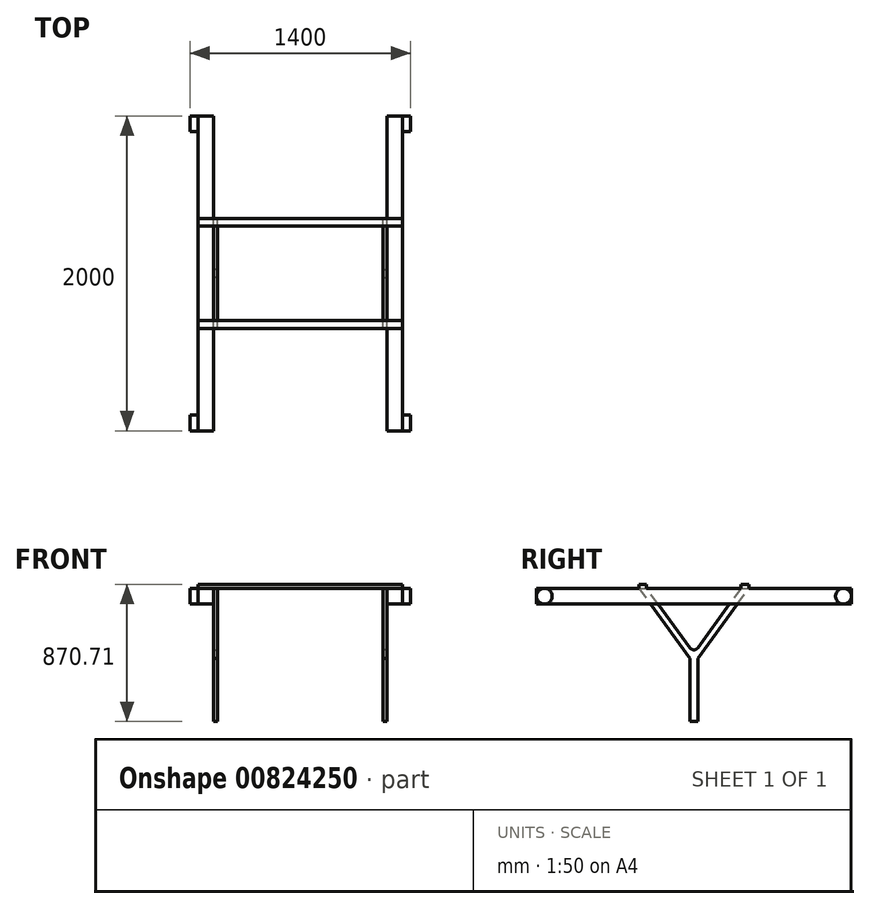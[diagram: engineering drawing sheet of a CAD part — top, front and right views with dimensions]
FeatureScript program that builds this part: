
annotation { "Feature Type Name" : "Feature", "Feature Type Description" : "" }
export const myFeature = defineFeature(function(context is Context, id is Id, definition is map)
    precondition{}
    {
        {
            var Q0;
            Q0=qCreatedBy(makeId("Top.planeOp"),FACE);
            var sketch = newSketch(context, id + "F0", { "sketchPlane" : qUnion([Q0])});
            skLineSegment(sketch, "E0.bottom", {"start": v(650, -1000) * mm, "end": v(550, -1000) * mm});
            skLineSegment(sketch, "E0.top", {"start": v(650, 1000) * mm, "end": v(550, 1000) * mm});
            skLineSegment(sketch, "E0.left", {"start": v(650, -1000) * mm, "end": v(650, 1000) * mm});
            skLineSegment(sketch, "E0.right", {"start": v(-650, -1000) * mm, "end": v(-650, 1000) * mm});
            skPoint(sketch, "E0.middle", {"position": v(0, 0) * mm});
            skLineSegment(sketch, "E1.left", {"start": v(-550, -1000) * mm, "end": v(-550, 1000) * mm});
            skLineSegment(sketch, "E1.right", {"start": v(550, -1000) * mm, "end": v(550, 1000) * mm});
            skLineSegment(sketch, "E2.trimOffspring", {"start": v(-550, 1000) * mm, "end": v(-650, 1000) * mm});
            skLineSegment(sketch, "E3.trimOffspring", {"start": v(-550, -1000) * mm, "end": v(-650, -1000) * mm});
            skSolve(sketch);
        }
        {
            var Q0;
            Q0 = qSketchRegion(id + "F0", true);
            extrude(context, id + "F1", {"entities" : qUnion([Q0]), "depth" : 100 * mm, "offsetDistance" : 25 * mm});
        }
        {
            var Q0;
            Q0=makeQuery(id+"F1.opExtrude","CAP_FACE",FACE,{"disambiguationData":[OSD([sQuery(id+"F0.wireOp",EDGE,"E0.bottom"),sQuery(id+"F0.wireOp",EDGE,"E0.top"),sQuery(id+"F0.wireOp",EDGE,"E0.left"),sQuery(id+"F0.wireOp",EDGE,"E1.right")])],"isStart":false});
            var sketch = newSketch(context, id + "F2", { "sketchPlane" : qUnion([Q0])});
            skLineSegment(sketch, "E4.bottom", {"start": v(650, -350) * mm, "end": v(-650, -350) * mm});
            skLineSegment(sketch, "E4.top", {"start": v(650, -300) * mm, "end": v(-650, -300) * mm});
            skLineSegment(sketch, "E4.left", {"start": v(650, -350) * mm, "end": v(650, -300) * mm});
            skLineSegment(sketch, "E4.right", {"start": v(-650, -350) * mm, "end": v(-650, -300) * mm});
            skLineSegment(sketch, "E5.MirrorCS", {"start": v(-650, 350) * mm, "end": v(-650, 300) * mm});
            skLineSegment(sketch, "E6.MirrorCS", {"start": v(650, 350) * mm, "end": v(650, 300) * mm});
            skLineSegment(sketch, "E7.MirrorCS", {"start": v(650, 300) * mm, "end": v(-650, 300) * mm});
            skLineSegment(sketch, "E8.MirrorCS", {"start": v(650, 350) * mm, "end": v(-650, 350) * mm});
            skSolve(sketch);
        }
        {
            var Q0;
            Q0 = qSketchRegion(id + "F2", true);
            extrude(context, id + "F3", {"entities" : qUnion([Q0]), "operationType" : NewBodyOperationType.ADD, "depth" : 25 * mm, "offsetDistance" : 25 * mm});
        }
        {
            var Q0;
            Q0=makeQuery(id+"F3.boolean.opBoolean","MERGE",FACE,{"derivedFrom":[makeQuery(id+"F1.opExtrude","SWEPT_FACE",FACE,{"disambiguationData":[OSD([sQuery(id+"F0.wireOp",EDGE,"E0.left")])]}),makeQuery(id+"F3.opExtrude","SWEPT_FACE",FACE,{"disambiguationData":[OSD([sQuery(id+"F2.wireOp",EDGE,"E4.left")])]}),makeQuery(id+"F3.opExtrude","SWEPT_FACE",FACE,{"disambiguationData":[OSD([sQuery(id+"F2.wireOp",EDGE,"E6.MirrorCS")])]})]});
            var sketch = newSketch(context, id + "F4", { "sketchPlane" : qUnion([Q0])});
            skCircle(sketch, "E9", {"center": v(-950, 50) * mm, "radius": 50 * mm});
            skCircle(sketch, "E10", {"center": v(950, 50) * mm, "radius": 50 * mm});
            skSolve(sketch);
        }
        {
            var Q0;
            Q0 = qSketchRegion(id + "F4", true);
            extrude(context, id + "F5", {"entities" : qUnion([Q0]), "operationType" : NewBodyOperationType.ADD, "depth" : 50 * mm, "offsetDistance" : 25 * mm});
        }
        {
            var Q0;
            Q0=makeQuery(id+"F3.boolean.opBoolean","MERGE",FACE,{"derivedFrom":[makeQuery(id+"F1.opExtrude","SWEPT_FACE",FACE,{"disambiguationData":[OSD([sQuery(id+"F0.wireOp",EDGE,"E0.right")])]}),makeQuery(id+"F3.opExtrude","SWEPT_FACE",FACE,{"disambiguationData":[OSD([sQuery(id+"F2.wireOp",EDGE,"E4.right")])]}),makeQuery(id+"F3.opExtrude","SWEPT_FACE",FACE,{"disambiguationData":[OSD([sQuery(id+"F2.wireOp",EDGE,"E5.MirrorCS")])]})]});
            var sketch = newSketch(context, id + "F6", { "sketchPlane" : qUnion([Q0])});
            skCircle(sketch, "E11.0", {"center": v(-950, 50) * mm, "radius": 50 * mm});
            skCircle(sketch, "E12.0", {"center": v(950, 50) * mm, "radius": 50 * mm});
            skSolve(sketch);
        }
        {
            var Q0;
            Q0 = qSketchRegion(id + "F6", true);
            extrude(context, id + "F7", {"entities" : qUnion([Q0]), "operationType" : NewBodyOperationType.ADD, "depth" : 50 * mm, "offsetDistance" : 25 * mm});
        }
        {
            var Q0;
            Q0=makeQuery(id+"F1.opExtrude","SWEPT_FACE",FACE,{"disambiguationData":[OSD([sQuery(id+"F0.wireOp",EDGE,"E1.left")])]});
            var sketch = newSketch(context, id + "F8", { "sketchPlane" : qUnion([Q0])});
            skLineSegment(sketch, "E13", {"start": v(-350, 100) * mm, "end": v(-25, -345.71) * mm});
            skLineSegment(sketch, "E14", {"start": v(25, -345.71) * mm, "end": v(350, 100) * mm});
            skLineSegment(sketch, "E15", {"start": v(350, 100) * mm, "end": v(300, 100) * mm});
            skLineSegment(sketch, "E16", {"start": v(300, 100) * mm, "end": v(0, -311.43) * mm});
            skLineSegment(sketch, "E17", {"start": v(0, -311.43) * mm, "end": v(-300, 100) * mm});
            skLineSegment(sketch, "E18", {"start": v(-300, 100) * mm, "end": v(-350, 100) * mm});
            skLineSegment(sketch, "E19.top", {"start": v(-25, -745.71) * mm, "end": v(25, -745.71) * mm});
            skLineSegment(sketch, "E19.left", {"start": v(-25, -345.71) * mm, "end": v(-25, -745.71) * mm});
            skLineSegment(sketch, "E19.right", {"start": v(25, -345.71) * mm, "end": v(25, -745.71) * mm});
            skPoint(sketch, "E20.orphan", {"position": v(0, -380) * mm});
            skSolve(sketch);
        }
        {
            var Q0;
            Q0 = qSketchRegion(id + "F8", true);
            extrude(context, id + "F9", {"entities" : qUnion([Q0]), "operationType" : NewBodyOperationType.ADD, "depth" : 25 * mm, "offsetDistance" : 25 * mm});
        }
        {
            var Q0;
            Q0=makeQuery(id+"F1.opExtrude","SWEPT_FACE",FACE,{"disambiguationData":[OSD([sQuery(id+"F0.wireOp",EDGE,"E1.right")])]});
            var sketch = newSketch(context, id + "F10", { "sketchPlane" : qUnion([Q0])});
            skLineSegment(sketch, "E21.0.0", {"start": v(350, 100) * mm, "end": v(25, -345.71) * mm});
            skLineSegment(sketch, "E21.0.1", {"start": v(-25, -345.71) * mm, "end": v(-350, 100) * mm});
            skLineSegment(sketch, "E21.0.2", {"start": v(-350, 100) * mm, "end": v(-300, 100) * mm});
            skLineSegment(sketch, "E21.0.3", {"start": v(-300, 100) * mm, "end": v(0, -311.43) * mm});
            skLineSegment(sketch, "E21.0.4", {"start": v(0, -311.43) * mm, "end": v(300, 100) * mm});
            skLineSegment(sketch, "E21.0.5", {"start": v(300, 100) * mm, "end": v(350, 100) * mm});
            skLineSegment(sketch, "E22.0", {"start": v(25, -345.71) * mm, "end": v(25, -745.71) * mm});
            skLineSegment(sketch, "E23.0", {"start": v(-25, -345.71) * mm, "end": v(-25, -745.71) * mm});
            skPoint(sketch, "E24.0", {"position": v(0, -745.71) * mm});
            skLineSegment(sketch, "E25.0", {"start": v(25, -745.71) * mm, "end": v(-25, -745.71) * mm});
            skSolve(sketch);
        }
        {
            var Q0;
            Q0 = qSketchRegion(id + "F10", true);
            extrude(context, id + "F11", {"entities" : qUnion([Q0]), "operationType" : NewBodyOperationType.ADD, "depth" : 25 * mm, "offsetDistance" : 25 * mm});
        }
        {
            var Q0;
            Q0=makeQuery(id+"F9.opExtrude","SWEPT_EDGE",EDGE,{"disambiguationData":[OSD([sQuery(id+"F8.wireOp",EDGE,"E16"),sQuery(id+"F8.wireOp",EDGE,"E17")])]});
            var Q1;
            Q1=makeQuery(id+"F11.opExtrude","SWEPT_EDGE",EDGE,{"disambiguationData":[OSD([sQuery(id+"F10.wireOp",EDGE,"E21.0.3"),sQuery(id+"F10.wireOp",EDGE,"E21.0.4")])]});
            fillet(context, id + "F12", {"entities" : qUnion([Q0, Q1]), "radius" : 30 * mm, "tangentPropagation" : true, "allowEdgeOverflow" : false});
        }
    });
